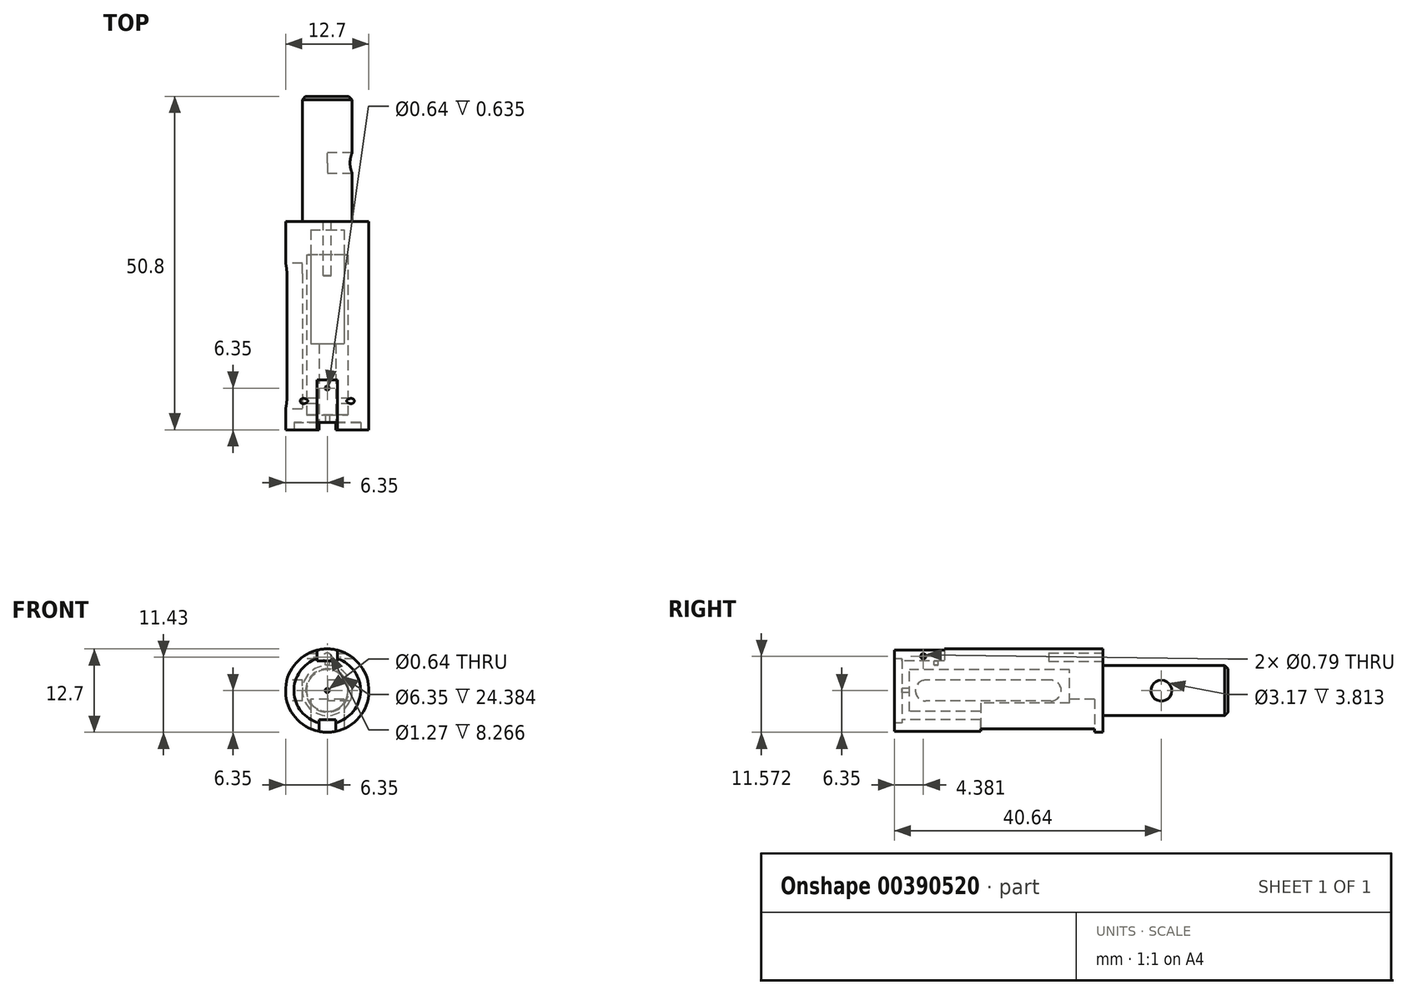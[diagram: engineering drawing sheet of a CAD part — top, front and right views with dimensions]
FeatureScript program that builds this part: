
annotation { "Feature Type Name" : "Feature", "Feature Type Description" : "" }
export const myFeature = defineFeature(function(context is Context, id is Id, definition is map)
    precondition{}
    {
        {
            var Q0;
            Q0=qCreatedBy(makeId("Right.planeOp"),FACE);
            var sketch = newSketch(context, id + "F0", { "sketchPlane" : qUnion([Q0])});
            skLineSegment(sketch, "E0.bottom", {"start": v(26.67, 0) * mm, "end": v(50.8, 0) * mm});
            skLineSegment(sketch, "E0.top", {"start": v(0, 6.35) * mm, "end": v(31.75, 6.35) * mm});
            skLineSegment(sketch, "E0.left", {"start": v(0, 5.08) * mm, "end": v(0, 6.35) * mm});
            skLineSegment(sketch, "E0.right", {"start": v(50.8, 0) * mm, "end": v(50.8, 3.81) * mm});
            skLineSegment(sketch, "E1", {"start": v(31.75, 6.35) * mm, "end": v(31.75, 3.81) * mm});
            skLineSegment(sketch, "E2", {"start": v(31.75, 3.81) * mm, "end": v(50.8, 3.81) * mm});
            skPoint(sketch, "E2.endSnap0", {"position": v(50.8, 3.18) * mm});
            skPoint(sketch, "E3.orphan", {"position": v(50.8, 6.35) * mm});
            skLineSegment(sketch, "E4", {"start": v(0, 5.08) * mm, "end": v(1.14, 5.08) * mm});
            skLineSegment(sketch, "E5", {"start": v(1.14, 5.08) * mm, "end": v(1.14, 0.32) * mm});
            skPoint(sketch, "E6.orphan", {"position": v(0, 0) * mm});
            skLineSegment(sketch, "E7", {"start": v(1.14, 0.32) * mm, "end": v(2.29, 0.32) * mm});
            skLineSegment(sketch, "E8", {"start": v(2.29, 0.32) * mm, "end": v(2.29, 3.18) * mm});
            skLineSegment(sketch, "E9", {"start": v(2.29, 3.18) * mm, "end": v(26.67, 3.18) * mm});
            skLineSegment(sketch, "E10", {"start": v(26.67, 3.18) * mm, "end": v(26.67, 0) * mm});
            skPoint(sketch, "E11.orphan", {"position": v(1.14, 0) * mm});
            skSolve(sketch);
        }
        {
            var Q0;
            Q0=makeQuery(id+"F0.imprint","IMPRINT",FACE,{"disambiguationData":[TD([[makeQuery(id+"F0.imprint","IMPRINT",EDGE,{"derivedFrom":sQuery(id+"F0.wireOp",EDGE,"E0.top")}),-1.0]])]});
            var Q1;
            Q1=sQuery(id+"F0.wireOp",EDGE,"E0.bottom");
            revolve(context, id + "F1", {"entities" : qUnion([Q0]), "axis" : qUnion([Q1]), "revolveType" : RevolveType.FULL});
        }
        {
            var Q0;
            Q0=qCreatedBy(makeId("Right.planeOp"),FACE);
            var sketch = newSketch(context, id + "F2", { "sketchPlane" : qUnion([Q0])});
            skCircle(sketch, "E12", {"center": v(40.64, 0) * mm, "radius": 1.59 * mm});
            skSolve(sketch);
        }
        {
            var Q0;
            Q0 = qSketchRegion(id + "F2", true);
            extrude(context, id + "F3", {"entities" : qUnion([Q0]), "operationType" : NewBodyOperationType.REMOVE, "depth" : 25.4 * mm});
        }
        {
            var Q0;
            Q0=qCreatedBy(makeId("Right.planeOp"),FACE);
            cPlane(context, id + "F4", {"entities" : qUnion([Q0]), "cplaneType" : CPlaneType.OFFSET, "offset" : 6.35 * mm, "oppositeDirection" : true, "width" : 152.4 * mm, "height" : 152.4 * mm});
        }
        {
            var Q0;
            Q0=qCreatedBy(id+"F4.planeOp",FACE);
            var sketch = newSketch(context, id + "F5", { "sketchPlane" : qUnion([Q0])});
            skArc(sketch, "E13", {"start": v(23.81, -1.59) * mm, "mid": v(25.4, 0) * mm, "end": v(23.81, 1.59) * mm});
            skArc(sketch, "E14", {"start": v(4.76, 1.59) * mm, "mid": v(3.17, 0) * mm, "end": v(4.76, -1.59) * mm});
            skLineSegment(sketch, "E15", {"start": v(23.81, 1.59) * mm, "end": v(4.76, 1.59) * mm});
            skLineSegment(sketch, "E16", {"start": v(4.76, -1.59) * mm, "end": v(23.81, -1.59) * mm});
            skSolve(sketch);
        }
        {
            var Q0;
            Q0 = qSketchRegion(id + "F5", true);
            extrude(context, id + "F6", {"entities" : qUnion([Q0]), "operationType" : NewBodyOperationType.REMOVE, "depth" : 2.54 * mm});
        }
        {
            var Q0;
            Q0=qCreatedBy(makeId("Front.planeOp"),FACE);
            cPlane(context, id + "F7", {"entities" : qUnion([Q0]), "cplaneType" : CPlaneType.OFFSET, "offset" : 13.1 * mm, "oppositeDirection" : true, "width" : 152.4 * mm, "height" : 152.4 * mm});
        }
        {
            var Q0;
            Q0=qCreatedBy(id+"F7.planeOp",FACE);
            var sketch = newSketch(context, id + "F8", { "sketchPlane" : qUnion([Q0])});
            skLineSegment(sketch, "E17.bottom", {"start": v(-2.54, -1.31) * mm, "end": v(2.54, -1.31) * mm});
            skLineSegment(sketch, "E17.top", {"start": v(-2.54, -14.01) * mm, "end": v(2.54, -14.01) * mm});
            skLineSegment(sketch, "E17.left", {"start": v(-2.54, -1.31) * mm, "end": v(-2.54, -14.01) * mm});
            skLineSegment(sketch, "E17.right", {"start": v(2.54, -1.31) * mm, "end": v(2.54, -14.01) * mm});
            skSolve(sketch);
        }
        {
            var Q0;
            Q0 = qSketchRegion(id + "F8", true);
            extrude(context, id + "F9", {"entities" : qUnion([Q0]), "operationType" : NewBodyOperationType.REMOVE, "oppositeDirection" : true, "depth" : 17.35 * mm});
        }
        {
            var Q0;
            Q0=makeQuery(id+"F1.opRevolve","SWEPT_FACE",FACE,{"disambiguationData":[OSD([sQuery(id+"F0.wireOp",EDGE,"E0.left")])]});
            var sketch = newSketch(context, id + "F10", { "sketchPlane" : qUnion([Q0])});
            skLineSegment(sketch, "E18.bottom", {"start": v(-1.59, 7.69) * mm, "end": v(1.59, 7.69) * mm});
            skLineSegment(sketch, "E18.top", {"start": v(-1.59, 4.51) * mm, "end": v(1.59, 4.51) * mm});
            skLineSegment(sketch, "E18.left", {"start": v(-1.59, 7.69) * mm, "end": v(-1.59, 4.51) * mm});
            skLineSegment(sketch, "E18.right", {"start": v(1.59, 7.69) * mm, "end": v(1.59, 4.51) * mm});
            skSolve(sketch);
        }
        {
            var Q0;
            Q0 = qSketchRegion(id + "F10", true);
            extrude(context, id + "F11", {"entities" : qUnion([Q0]), "operationType" : NewBodyOperationType.REMOVE, "oppositeDirection" : true, "depth" : 7.62 * mm});
        }
        {
            var Q0;
            Q0=makeQuery(id+"F11.boolean.opBoolean","COPY",FACE,{"derivedFrom":makeQuery(id+"F11.opExtrude","SWEPT_FACE",FACE,{"disambiguationData":[OSD([sQuery(id+"F10.wireOp",EDGE,"E18.right")])]})});
            var sketch = newSketch(context, id + "F12", { "sketchPlane" : qUnion([Q0])});
            skCircle(sketch, "E19", {"center": v(-4.38, 5.22) * mm, "radius": 0.4 * mm});
            skPoint(sketch, "E19.centerSnap0", {"position": v(-4.38, 4.51) * mm});
            skSolve(sketch);
        }
        {
            var Q0;
            Q0 = qSketchRegion(id + "F12", true);
            extrude(context, id + "F13", {"entities" : qUnion([Q0]), "operationType" : NewBodyOperationType.REMOVE, "oppositeDirection" : true, "depth" : 25.4 * mm, "hasSecondDirection" : true, "secondDirectionOppositeDirection" : false, "secondDirectionDepth" : 25.4 * mm});
        }
        {
            var Q0;
            Q0=makeQuery(id+"F11.boolean.opBoolean","COPY",FACE,{"derivedFrom":makeQuery(id+"F11.opExtrude","SWEPT_FACE",FACE,{"disambiguationData":[OSD([sQuery(id+"F10.wireOp",EDGE,"E18.top")])]})});
            var sketch = newSketch(context, id + "F14", { "sketchPlane" : qUnion([Q0])});
            skCircle(sketch, "E20", {"center": v(0, 6.35) * mm, "radius": 0.32 * mm});
            skSolve(sketch);
        }
        {
            var Q0;
            Q0 = qSketchRegion(id + "F14", true);
            extrude(context, id + "F15", {"entities" : qUnion([Q0]), "operationType" : NewBodyOperationType.REMOVE, "oppositeDirection" : true, "depth" : 0.64 * mm});
        }
        {
            var Q0;
            Q0=makeQuery(id+"F1.opRevolve","SWEPT_FACE",FACE,{"disambiguationData":[OSD([sQuery(id+"F0.wireOp",EDGE,"E1")])]});
            var sketch = newSketch(context, id + "F16", { "sketchPlane" : qUnion([Q0])});
            skCircle(sketch, "E21", {"center": v(0, 5.08) * mm, "radius": 0.64 * mm});
            skSolve(sketch);
        }
        {
            var Q0;
            Q0 = qSketchRegion(id + "F16", true);
            extrude(context, id + "F17", {"entities" : qUnion([Q0]), "operationType" : NewBodyOperationType.REMOVE, "oppositeDirection" : true, "depth" : 8.27 * mm});
        }
        {
            var Q0;
            Q0=makeQuery(id+"F1.opRevolve","SWEPT_FACE",FACE,{"disambiguationData":[OSD([sQuery(id+"F0.wireOp",EDGE,"E0.left")])]});
            var sketch = newSketch(context, id + "F18", { "sketchPlane" : qUnion([Q0])});
            skLineSegment(sketch, "E22.bottom", {"start": v(-1.27, -8.32) * mm, "end": v(1.27, -8.32) * mm});
            skLineSegment(sketch, "E22.top", {"start": v(-1.27, -4.45) * mm, "end": v(1.27, -4.45) * mm});
            skLineSegment(sketch, "E22.left", {"start": v(-1.27, -8.32) * mm, "end": v(-1.27, -4.45) * mm});
            skLineSegment(sketch, "E22.right", {"start": v(1.27, -8.32) * mm, "end": v(1.27, -4.45) * mm});
            skSolve(sketch);
        }
        {
            var Q0;
            Q0 = qSketchRegion(id + "F18", true);
            extrude(context, id + "F19", {"entities" : qUnion([Q0]), "operationType" : NewBodyOperationType.REMOVE, "oppositeDirection" : true, "depth" : 25.4 * mm});
        }
        {
            var Q0;
            Q0=makeQuery(id+"F1.opRevolve","SWEPT_EDGE",EDGE,{"disambiguationData":[OSD([sQuery(id+"F0.wireOp",EDGE,"E0.right"),sQuery(id+"F0.wireOp",EDGE,"E2")])]});
            chamfer(context, id + "F20", {"entities" : qUnion([Q0]), "width" : 0.5 * mm, "tangentPropagation" : true});
        }
    });
